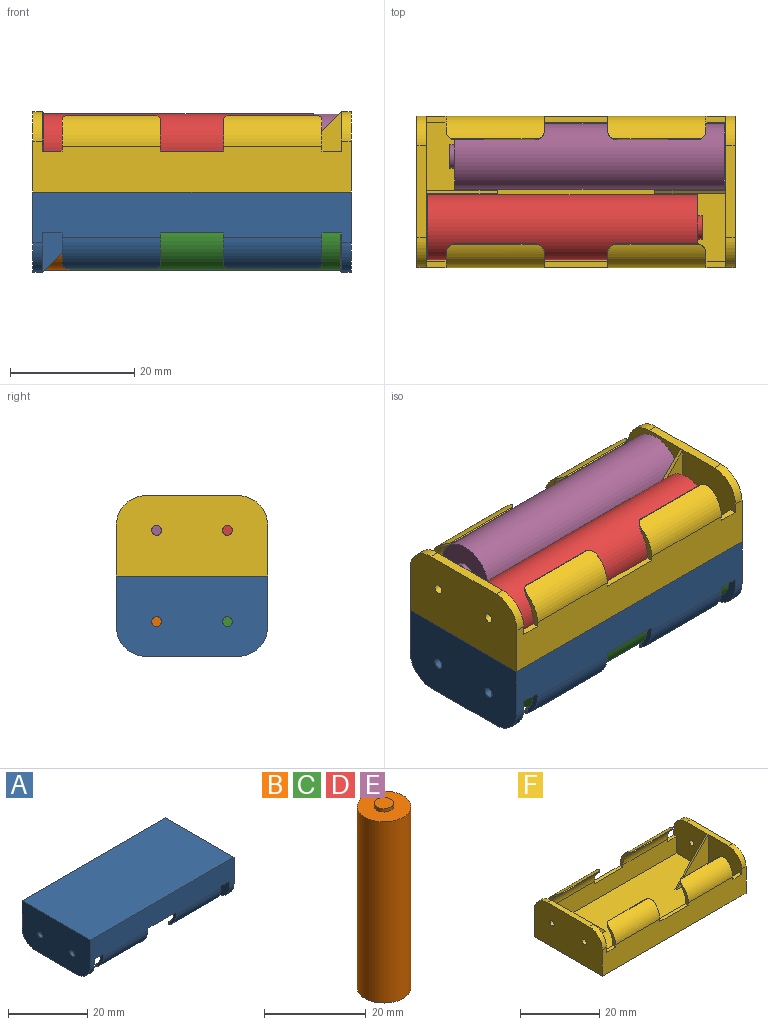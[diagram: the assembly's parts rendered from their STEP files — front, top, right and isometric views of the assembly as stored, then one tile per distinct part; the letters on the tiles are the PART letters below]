
ASSEMBLY  parts=6 mates=8
PART A: 62 faces, bbox 51.3x24.4x13 mm
  f0: plane 51.31x8.19mm, normal (0,-1,0), area 367.9mm2, adj f1,f15,f17,f18,f22,f24,f25,f30
  f1: cylinder r=5.2mm len=15.88mm, axis (-1,0,0), area 103.8mm2, adj f0,f2,f52,f53,f56,f58
  f2: cylinder r=0.13mm len=14.16mm, axis (-1,0,0), area 5mm2, adj f1,f3,f53,f58
  f3: cylinder r=5.46mm len=15.88mm, axis (-1,0,0), area 89.7mm2, adj f2,f4,f52,f53,f56,f58
  f4: plane 48.26x5.84mm, normal (0,1,0), area 269.4mm2, adj f3,f14,f24,f30,f39,f51,f52,f54
  f5: cylinder r=0.13mm len=14.16mm, axis (-1,0,0), area 5mm2, adj f7,f10,f41,f43
  f6: cylinder r=0.13mm len=14.16mm, axis (-1,0,0), area 5mm2, adj f8,f11,f46,f48
  f7: cylinder r=5.2mm len=15.88mm, axis (-1,0,0), area 103.8mm2, adj f5,f16,f40,f41,f43,f44
  f8: cylinder r=5.2mm len=15.88mm, axis (-1,0,0), area 103.8mm2, adj f6,f16,f45,f46,f48,f49
  f9: plane 48.26x5.84mm, normal (0,-1,0), area 269.4mm2, adj f10,f11,f12,f13,f14,f40,f42,f44
  f10: cylinder r=5.46mm len=15.88mm, axis (-1,0,0), area 89.7mm2, adj f5,f9,f40,f41,f43,f44
  f11: cylinder r=5.46mm len=15.88mm, axis (-1,0,0), area 89.7mm2, adj f6,f9,f45,f46,f48,f49
  f12: plane 11.94x11.43mm, normal (-1,0,0), area 124.4mm2, adj f9,f14,f16,f19,f20,f23,f36,f50
  f13: plane 11.94x11.43mm, normal (1,0,0), area 124.4mm2, adj f9,f14,f16,f26,f27,f28,f33,f42
  f14: plane 48.26x22.35mm, normal (0,0,-1), area 1067.1mm2, adj f4,f9,f12,f13,f24,f30,f31,f32
  f15: plane 24.38x12.95mm, normal (1,0,0), area 302.2mm2, adj f0,f16,f18,f19,f20,f21,f22,f23
  f16: plane 51.31x8.19mm, normal (0,1,0), area 367.9mm2, adj f7,f8,f12,f13,f15,f17,f18,f19
  f17: plane 24.38x12.95mm, normal (-1,0,0), area 302.2mm2, adj f0,f16,f18,f25,f26,f27,f28,f29
  f18: plane 51.31x24.38mm, normal (0,0,1), area 1251.1mm2, adj f0,f15,f16,f17
  f19: cylinder r=4.76mm len=4.76mm, axis (1,0,0), area 11.4mm2, adj f12,f15,f16,f20
  f20: plane 14.86x1.52mm, normal (0,0,-1), area 22.6mm2, adj f12,f15,f19,f22,f24,f34
  f21: cylinder r=0.79mm len=1.59mm, axis (1,0,0), area 7.6mm2, adj f15,f24
  f22: cylinder r=4.76mm len=4.76mm, axis (1,0,0), area 11.4mm2, adj f0,f15,f20,f24
  f23: cylinder r=0.79mm len=1.59mm, axis (1,0,0), area 7.6mm2, adj f12,f15
  f24: plane 11.94x11.43mm, normal (-1,0,0), area 124.4mm2, adj f0,f4,f14,f20,f21,f22,f35,f60
  f25: cylinder r=4.76mm len=4.76mm, axis (-1,0,0), area 11.4mm2, adj f0,f17,f26,f30
  f26: plane 14.86x1.52mm, normal (0,0,-1), area 22.6mm2, adj f13,f17,f25,f27,f30,f31
  f27: cylinder r=4.76mm len=4.76mm, axis (-1,0,0), area 11.4mm2, adj f13,f16,f17,f26
  f28: cylinder r=0.79mm len=1.59mm, axis (-1,0,0), area 7.6mm2, adj f13,f17
  f29: cylinder r=0.79mm len=1.59mm, axis (-1,0,0), area 7.6mm2, adj f17,f30
  f30: plane 11.94x11.43mm, normal (1,0,0), area 124.4mm2, adj f0,f4,f14,f25,f26,f29,f32,f51
  f31: plane 11.43x11.43mm, normal (0.71,0,-0.71), area 8.2mm2, adj f14,f26,f32,f33
  f32: plane 11.43x11.43mm, normal (0,-1,0), area 65.3mm2, adj f14,f30,f31
  f33: plane 11.43x11.43mm, normal (0,1,0), area 65.3mm2, adj f13,f14,f31
  f34: plane 11.43x11.43mm, normal (-0.71,0,-0.71), area 8.2mm2, adj f14,f20,f35,f36
  f35: plane 11.43x11.43mm, normal (0,-1,0), area 65.3mm2, adj f14,f24,f34
  f36: plane 11.43x11.43mm, normal (0,1,0), area 65.3mm2, adj f12,f14,f34
  f37: cylinder r=5.2mm len=15.88mm, axis (-1,0,0), area 103.8mm2, adj f0,f38,f55,f57,f59,f61
  f38: cylinder r=0.13mm len=14.16mm, axis (-1,0,0), area 5mm2, adj f37,f39,f57,f61
  f39: cylinder r=5.46mm len=15.88mm, axis (-1,0,0), area 89.7mm2, adj f4,f38,f55,f57,f59,f61
  f40: plane 5.03x2.24mm, normal (-1,0,0), area 4.6mm2, adj f7,f9,f10,f16,f41,f42
  f41: cylinder r=1.59mm len=1.57mm, axis (0,0,-1), area 1mm2, adj f5,f7,f10,f40
  f42: plane 3.18x1.02mm, normal (0,0,-1), area 3.2mm2, adj f9,f13,f16,f40
  f43: cylinder r=1.59mm len=1.57mm, axis (0,0,-1), area 1mm2, adj f5,f7,f10,f44
  f44: plane 5.03x2.24mm, normal (1,0,0), area 4.6mm2, adj f7,f9,f10,f16,f43,f47
  f45: plane 5.03x2.24mm, normal (-1,0,0), area 4.6mm2, adj f8,f9,f11,f16,f46,f47
  f46: cylinder r=1.59mm len=1.57mm, axis (0,0,-1), area 1mm2, adj f6,f8,f11,f45
  f47: plane 10.16x1.02mm, normal (0,0,-1), area 10.3mm2, adj f9,f16,f44,f45
  f48: cylinder r=1.59mm len=1.57mm, axis (0,0,-1), area 1mm2, adj f6,f8,f11,f49
  f49: plane 5.03x2.24mm, normal (1,0,0), area 4.6mm2, adj f8,f9,f11,f16,f48,f50
  f50: plane 3.18x1.02mm, normal (0,0,-1), area 3.2mm2, adj f9,f12,f16,f49
  f51: plane 3.18x1.02mm, normal (0,0,-1), area 3.2mm2, adj f0,f4,f30,f52
  f52: plane 5.03x2.24mm, normal (-1,0,0), area 4.6mm2, adj f0,f1,f3,f4,f51,f53
  f53: cylinder r=1.59mm len=1.57mm, axis (0,0,-1), area 1mm2, adj f1,f2,f3,f52
  f54: plane 10.16x1.02mm, normal (0,0,-1), area 10.3mm2, adj f0,f4,f55,f56
  f55: plane 5.03x2.24mm, normal (-1,0,0), area 4.6mm2, adj f0,f4,f37,f39,f54,f57
  f56: plane 5.03x2.24mm, normal (1,0,0), area 4.6mm2, adj f0,f1,f3,f4,f54,f58
  f57: cylinder r=1.59mm len=1.57mm, axis (0,0,-1), area 1mm2, adj f37,f38,f39,f55
  f58: cylinder r=1.59mm len=1.57mm, axis (0,0,-1), area 1mm2, adj f1,f2,f3,f56
  f59: plane 5.03x2.24mm, normal (1,0,0), area 4.6mm2, adj f0,f4,f37,f39,f60,f61
  f60: plane 3.18x1.02mm, normal (0,0,-1), area 3.2mm2, adj f0,f4,f24,f59
  f61: cylinder r=1.59mm len=1.57mm, axis (0,0,-1), area 1mm2, adj f37,f38,f39,f59
PART B: 7 faces, bbox 10.5x10.5x44.5 mm
  f0: plane 4.3x4.3mm, normal (0,0,-1), area 14.5mm2, adj f1
  f1: cylinder r=2.15mm len=4.3mm, axis (0,0,1), area 2.7mm2, adj f0,f2
  f2: plane 10.5x10.5mm, normal (0,0,-1), area 72.1mm2, adj f1,f3
  f3: cylinder r=5.25mm len=43.5mm, axis (0,0,1), area 1434.9mm2, adj f2,f4
  f4: plane 10.5x10.5mm, normal (0,0,1), area 75.2mm2, adj f3,f5
  f5: cylinder r=1.9mm len=3.8mm, axis (0,0,1), area 9.6mm2, adj f4,f6
  f6: plane 3.8x3.8mm, normal (0,0,1), area 11.3mm2, adj f5
PART C: same geometry as B
PART D: same geometry as B
PART E: same geometry as B
PART F: 62 faces, bbox 51.3x24.4x13 mm
  f0: plane 51.31x8.19mm, normal (0,-1,0), area 367.9mm2, adj f1,f15,f17,f18,f22,f24,f25,f30
  f1: cylinder r=5.2mm len=15.88mm, axis (-1,0,0), area 103.8mm2, adj f0,f2,f52,f53,f56,f58
  f2: cylinder r=0.13mm len=14.16mm, axis (-1,0,0), area 5mm2, adj f1,f3,f53,f58
  f3: cylinder r=5.46mm len=15.88mm, axis (-1,0,0), area 89.7mm2, adj f2,f4,f52,f53,f56,f58
  f4: plane 48.26x5.84mm, normal (0,1,0), area 269.4mm2, adj f3,f14,f24,f30,f39,f51,f52,f54
  f5: cylinder r=0.13mm len=14.16mm, axis (-1,0,0), area 5mm2, adj f7,f10,f41,f43
  f6: cylinder r=0.13mm len=14.16mm, axis (-1,0,0), area 5mm2, adj f8,f11,f46,f48
  f7: cylinder r=5.2mm len=15.88mm, axis (-1,0,0), area 103.8mm2, adj f5,f16,f40,f41,f43,f44
  f8: cylinder r=5.2mm len=15.88mm, axis (-1,0,0), area 103.8mm2, adj f6,f16,f45,f46,f48,f49
  f9: plane 48.26x5.84mm, normal (0,-1,0), area 269.4mm2, adj f10,f11,f12,f13,f14,f40,f42,f44
  f10: cylinder r=5.46mm len=15.88mm, axis (-1,0,0), area 89.7mm2, adj f5,f9,f40,f41,f43,f44
  f11: cylinder r=5.46mm len=15.88mm, axis (-1,0,0), area 89.7mm2, adj f6,f9,f45,f46,f48,f49
  f12: plane 11.94x11.43mm, normal (-1,0,0), area 124.4mm2, adj f9,f14,f16,f19,f20,f23,f36,f50
  f13: plane 11.94x11.43mm, normal (1,0,0), area 124.4mm2, adj f9,f14,f16,f26,f27,f28,f33,f42
  f14: plane 48.26x22.35mm, normal (0,0,1), area 1067.1mm2, adj f4,f9,f12,f13,f24,f30,f31,f32
  f15: plane 24.38x12.95mm, normal (1,0,0), area 302.2mm2, adj f0,f16,f18,f19,f20,f21,f22,f23
  f16: plane 51.31x8.19mm, normal (0,1,0), area 367.9mm2, adj f7,f8,f12,f13,f15,f17,f18,f19
  f17: plane 24.38x12.95mm, normal (-1,0,0), area 302.2mm2, adj f0,f16,f18,f25,f26,f27,f28,f29
  f18: plane 51.31x24.38mm, normal (0,0,-1), area 1251.1mm2, adj f0,f15,f16,f17
  f19: cylinder r=4.76mm len=4.76mm, axis (1,0,0), area 11.4mm2, adj f12,f15,f16,f20
  f20: plane 14.86x1.52mm, normal (0,0,1), area 22.6mm2, adj f12,f15,f19,f22,f24,f34
  f21: cylinder r=0.79mm len=1.59mm, axis (1,0,0), area 7.6mm2, adj f15,f24
  f22: cylinder r=4.76mm len=4.76mm, axis (1,0,0), area 11.4mm2, adj f0,f15,f20,f24
  f23: cylinder r=0.79mm len=1.59mm, axis (1,0,0), area 7.6mm2, adj f12,f15
  f24: plane 11.94x11.43mm, normal (-1,0,0), area 124.4mm2, adj f0,f4,f14,f20,f21,f22,f35,f60
  f25: cylinder r=4.76mm len=4.76mm, axis (-1,0,0), area 11.4mm2, adj f0,f17,f26,f30
  f26: plane 14.86x1.52mm, normal (0,0,1), area 22.6mm2, adj f13,f17,f25,f27,f30,f31
  f27: cylinder r=4.76mm len=4.76mm, axis (-1,0,0), area 11.4mm2, adj f13,f16,f17,f26
  f28: cylinder r=0.79mm len=1.59mm, axis (-1,0,0), area 7.6mm2, adj f13,f17
  f29: cylinder r=0.79mm len=1.59mm, axis (-1,0,0), area 7.6mm2, adj f17,f30
  f30: plane 11.94x11.43mm, normal (1,0,0), area 124.4mm2, adj f0,f4,f14,f25,f26,f29,f32,f51
  f31: plane 11.43x11.43mm, normal (0.71,0,0.71), area 8.2mm2, adj f14,f26,f32,f33
  f32: plane 11.43x11.43mm, normal (0,-1,0), area 65.3mm2, adj f14,f30,f31
  f33: plane 11.43x11.43mm, normal (0,1,0), area 65.3mm2, adj f13,f14,f31
  f34: plane 11.43x11.43mm, normal (-0.71,0,0.71), area 8.2mm2, adj f14,f20,f35,f36
  f35: plane 11.43x11.43mm, normal (0,-1,0), area 65.3mm2, adj f14,f24,f34
  f36: plane 11.43x11.43mm, normal (0,1,0), area 65.3mm2, adj f12,f14,f34
  f37: cylinder r=5.2mm len=15.88mm, axis (-1,0,0), area 103.8mm2, adj f0,f38,f55,f57,f59,f61
  f38: cylinder r=0.13mm len=14.16mm, axis (-1,0,0), area 5mm2, adj f37,f39,f57,f61
  f39: cylinder r=5.46mm len=15.88mm, axis (-1,0,0), area 89.7mm2, adj f4,f38,f55,f57,f59,f61
  f40: plane 5.03x2.24mm, normal (-1,0,0), area 4.6mm2, adj f7,f9,f10,f16,f41,f42
  f41: cylinder r=1.59mm len=1.57mm, axis (0,0,1), area 1mm2, adj f5,f7,f10,f40
  f42: plane 3.18x1.02mm, normal (0,0,1), area 3.2mm2, adj f9,f13,f16,f40
  f43: cylinder r=1.59mm len=1.57mm, axis (0,0,1), area 1mm2, adj f5,f7,f10,f44
  f44: plane 5.03x2.24mm, normal (1,0,0), area 4.6mm2, adj f7,f9,f10,f16,f43,f47
  f45: plane 5.03x2.24mm, normal (-1,0,0), area 4.6mm2, adj f8,f9,f11,f16,f46,f47
  f46: cylinder r=1.59mm len=1.57mm, axis (0,0,1), area 1mm2, adj f6,f8,f11,f45
  f47: plane 10.16x1.02mm, normal (0,0,1), area 10.3mm2, adj f9,f16,f44,f45
  f48: cylinder r=1.59mm len=1.57mm, axis (0,0,1), area 1mm2, adj f6,f8,f11,f49
  f49: plane 5.03x2.24mm, normal (1,0,0), area 4.6mm2, adj f8,f9,f11,f16,f48,f50
  f50: plane 3.18x1.02mm, normal (0,0,1), area 3.2mm2, adj f9,f12,f16,f49
  f51: plane 3.18x1.02mm, normal (0,0,1), area 3.2mm2, adj f0,f4,f30,f52
  f52: plane 5.03x2.24mm, normal (-1,0,0), area 4.6mm2, adj f0,f1,f3,f4,f51,f53
  f53: cylinder r=1.59mm len=1.57mm, axis (0,0,1), area 1mm2, adj f1,f2,f3,f52
  f54: plane 10.16x1.02mm, normal (0,0,1), area 10.3mm2, adj f0,f4,f55,f56
  f55: plane 5.03x2.24mm, normal (-1,0,0), area 4.6mm2, adj f0,f4,f37,f39,f54,f57
  f56: plane 5.03x2.24mm, normal (1,0,0), area 4.6mm2, adj f0,f1,f3,f4,f54,f58
  f57: cylinder r=1.59mm len=1.57mm, axis (0,0,1), area 1mm2, adj f37,f38,f39,f55
  f58: cylinder r=1.59mm len=1.57mm, axis (0,0,1), area 1mm2, adj f1,f2,f3,f56
  f59: plane 5.03x2.24mm, normal (1,0,0), area 4.6mm2, adj f0,f4,f37,f39,f60,f61
  f60: plane 3.18x1.02mm, normal (0,0,1), area 3.2mm2, adj f0,f4,f24,f59
  f61: cylinder r=1.59mm len=1.57mm, axis (0,0,1), area 1mm2, adj f37,f38,f39,f59
PLACE A at identity fixed
PLACE B rot(axis=(0,1,0),90deg) t=(-24.13,5.72,-7.37)mm
PLACE C rot(axis=(0.71,0,-0.71),180deg) t=(24.13,-5.71,-7.37)mm
PLACE D rot(axis=(0.7,0.09,0.7),169.5deg) t=(-24.13,-5.71,7.37)mm
PLACE E rot(axis=(0.71,0,-0.71),180deg) t=(24.13,5.72,7.37)mm
PLACE F at identity fixed
MATE planar F.f12 <-> E.f1  axis (-1,0,0) through (24.13,0.25,7.24)mm
MATE cylindrical A.f3 <-> C.f1  axis (1,0,0) through (25.65,-5.71,-7.37)mm
MATE planar C.f1 <-> A.f24  axis (1,0,0) through (24.13,-5.71,-7.37)mm
MATE planar D.f1 <-> F.f30  axis (-1,0,0) through (-24.13,-5.71,7.37)mm
MATE cylindrical E.f1 <-> F.f10  axis (-1,0,0) through (2.18,5.72,7.37)mm
MATE planar B.f1 <-> A.f13  axis (-1,0,0) through (-24.13,5.72,-7.37)mm
MATE cylindrical B.f1 <-> A.f10  axis (1,0,0) through (-2.18,5.72,-7.37)mm
MATE cylindrical D.f1 <-> F.f3  axis (1,0,0) through (-2.18,-5.71,7.37)mm
